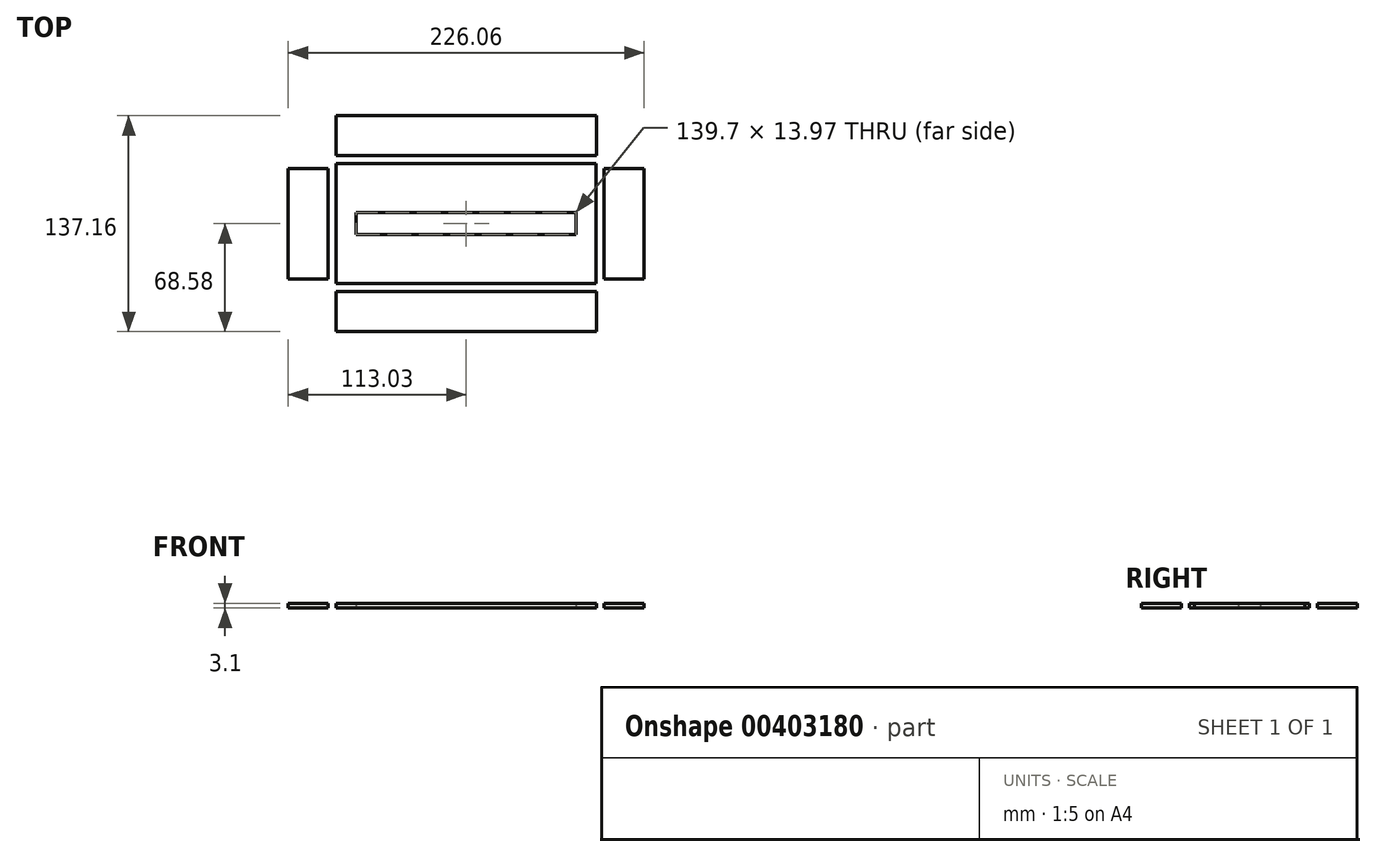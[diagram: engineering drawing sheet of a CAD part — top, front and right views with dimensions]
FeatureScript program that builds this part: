
annotation { "Feature Type Name" : "Feature", "Feature Type Description" : "" }
export const myFeature = defineFeature(function(context is Context, id is Id, definition is map)
    precondition{}
    {
        {
            var Q0;
            Q0=qCreatedBy(makeId("Top.planeOp"),FACE);
            var sketch = newSketch(context, id + "F0", { "sketchPlane" : qUnion([Q0])});
            skLineSegment(sketch, "E0.bottom", {"start": v(0, 0) * mm, "end": v(165.1, 0) * mm});
            skLineSegment(sketch, "E0.top", {"start": v(0, 76.2) * mm, "end": v(165.1, 76.2) * mm});
            skLineSegment(sketch, "E0.left", {"start": v(0, 0) * mm, "end": v(0, 76.2) * mm});
            skLineSegment(sketch, "E0.right", {"start": v(165.1, 0) * mm, "end": v(165.1, 76.2) * mm});
            skLineSegment(sketch, "E1.bottom", {"start": v(12.7, 45.09) * mm, "end": v(152.4, 45.09) * mm});
            skLineSegment(sketch, "E1.top", {"start": v(12.7, 31.12) * mm, "end": v(152.4, 31.12) * mm});
            skLineSegment(sketch, "E1.left", {"start": v(12.7, 45.09) * mm, "end": v(12.7, 31.12) * mm});
            skLineSegment(sketch, "E1.right", {"start": v(152.4, 45.09) * mm, "end": v(152.4, 31.12) * mm});
            skLineSegment(sketch, "E2", {"start": v(82.55, 45.09) * mm, "end": v(82.55, 31.12) * mm, "construction": true});
            skLineSegment(sketch, "E3", {"start": v(0, 38.1) * mm, "end": v(165.1, 38.1) * mm, "construction": true});
            skLineSegment(sketch, "E4", {"start": v(12.7, 38.1) * mm, "end": v(165.1, 38.1) * mm, "construction": true});
            skLineSegment(sketch, "E5", {"start": v(82.55, 0) * mm, "end": v(82.55, 76.2) * mm, "construction": true});
            skSolve(sketch);
        }
        {
            var Q0;
            Q0 = qSketchRegion(id + "F0", true);
            extrude(context, id + "F1", {"entities" : qUnion([Q0]), "depth" : 3.1 * mm});
        }
        {
            var Q0;
            Q0=makeQuery(id+"F1.opExtrude","CAP_FACE",FACE,{"disambiguationData":[OSD([sQuery(id+"F0.wireOp",EDGE,"E0.bottom"),sQuery(id+"F0.wireOp",EDGE,"E0.top"),sQuery(id+"F0.wireOp",EDGE,"E0.left"),sQuery(id+"F0.wireOp",EDGE,"E0.right"),sQuery(id+"F0.wireOp",EDGE,"E1.bottom"),sQuery(id+"F0.wireOp",EDGE,"E1.top"),sQuery(id+"F0.wireOp",EDGE,"E1.left"),sQuery(id+"F0.wireOp",EDGE,"E1.right")])],"isStart":false});
            var sketch = newSketch(context, id + "F2", { "sketchPlane" : qUnion([Q0])});
            skLineSegment(sketch, "E6.bottom", {"start": v(0, 76.2) * mm, "end": v(165.3, 76.2) * mm});
            skLineSegment(sketch, "E6.top", {"start": v(0, 106.68) * mm, "end": v(165.3, 106.68) * mm});
            skLineSegment(sketch, "E6.left", {"start": v(0, 81.28) * mm, "end": v(0, 106.68) * mm});
            skLineSegment(sketch, "E6.right", {"start": v(165.3, 81.28) * mm, "end": v(165.3, 106.68) * mm});
            skLineSegment(sketch, "E7.bottom", {"start": v(0, 0) * mm, "end": v(165.3, 0) * mm});
            skLineSegment(sketch, "E7.top", {"start": v(0, -30.48) * mm, "end": v(165.3, -30.48) * mm});
            skLineSegment(sketch, "E7.left", {"start": v(0, -5.08) * mm, "end": v(0, -30.48) * mm});
            skLineSegment(sketch, "E7.right", {"start": v(165.3, -5.08) * mm, "end": v(165.3, -30.48) * mm});
            skLineSegment(sketch, "E8.bottom", {"start": v(-5.08, 73.15) * mm, "end": v(-30.48, 73.15) * mm});
            skLineSegment(sketch, "E8.top", {"start": v(-5.08, 3.05) * mm, "end": v(-30.48, 3.05) * mm});
            skLineSegment(sketch, "E8.left", {"start": v(0, 73.15) * mm, "end": v(0, 3.05) * mm});
            skLineSegment(sketch, "E8.right", {"start": v(-30.48, 73.15) * mm, "end": v(-30.48, 3.05) * mm});
            skLineSegment(sketch, "E9.bottom", {"start": v(170.18, 3.05) * mm, "end": v(195.58, 3.05) * mm});
            skLineSegment(sketch, "E9.top", {"start": v(170.18, 73.15) * mm, "end": v(195.58, 73.15) * mm});
            skLineSegment(sketch, "E9.left", {"start": v(165.1, 3.05) * mm, "end": v(165.1, 73.15) * mm});
            skLineSegment(sketch, "E9.right", {"start": v(195.58, 3.05) * mm, "end": v(195.58, 73.15) * mm});
            skLineSegment(sketch, "E10", {"start": v(-5.08, 73.15) * mm, "end": v(-5.08, 3.05) * mm});
            skLineSegment(sketch, "E11", {"start": v(0, -5.08) * mm, "end": v(165.3, -5.08) * mm});
            skLineSegment(sketch, "E12", {"start": v(170.18, 3.05) * mm, "end": v(170.18, 73.15) * mm});
            skLineSegment(sketch, "E13", {"start": v(0, 81.28) * mm, "end": v(165.3, 81.28) * mm});
            skSolve(sketch);
        }
        {
            var Q0;
            Q0 = qSketchRegion(id + "F2", true);
            extrude(context, id + "F3", {"entities" : qUnion([Q0]), "oppositeDirection" : true, "depth" : 3.1 * mm});
        }
        {
            var Q0;
            Q0=makeQuery(id+"F3.opExtrude","SWEPT_BODY",BODY,{"disambiguationData":[OSD([sQuery(id+"F2.wireOp",EDGE,"E9.bottom"),sQuery(id+"F2.wireOp",EDGE,"E9.top"),sQuery(id+"F2.wireOp",EDGE,"E9.right"),sQuery(id+"F2.wireOp",EDGE,"E12")])]});
            var Q1;
            Q1=makeQuery(id+"F3.opExtrude","SWEPT_BODY",BODY,{"disambiguationData":[OSD([sQuery(id+"F2.wireOp",EDGE,"E8.bottom"),sQuery(id+"F2.wireOp",EDGE,"E8.top"),sQuery(id+"F2.wireOp",EDGE,"E8.right"),sQuery(id+"F2.wireOp",EDGE,"E10")])]});
            var Q2;
            Q2=makeQuery(id+"F3.opExtrude","SWEPT_BODY",BODY,{"disambiguationData":[OSD([sQuery(id+"F2.wireOp",EDGE,"E6.top"),sQuery(id+"F2.wireOp",EDGE,"E6.left"),sQuery(id+"F2.wireOp",EDGE,"E6.right"),sQuery(id+"F2.wireOp",EDGE,"E13")])]});
            var Q3;
            Q3=makeQuery(id+"F3.opExtrude","SWEPT_BODY",BODY,{"disambiguationData":[OSD([sQuery(id+"F2.wireOp",EDGE,"E7.top"),sQuery(id+"F2.wireOp",EDGE,"E7.left"),sQuery(id+"F2.wireOp",EDGE,"E7.right"),sQuery(id+"F2.wireOp",EDGE,"E11")])]});
            var Q4;
            Q4=makeQuery(id+"F1.opExtrude","SWEPT_BODY",BODY,{"disambiguationData":[OSD([sQuery(id+"F0.wireOp",EDGE,"E0.bottom"),sQuery(id+"F0.wireOp",EDGE,"E0.top"),sQuery(id+"F0.wireOp",EDGE,"E0.left"),sQuery(id+"F0.wireOp",EDGE,"E0.right"),sQuery(id+"F0.wireOp",EDGE,"E1.bottom"),sQuery(id+"F0.wireOp",EDGE,"E1.top"),sQuery(id+"F0.wireOp",EDGE,"E1.left"),sQuery(id+"F0.wireOp",EDGE,"E1.right")])]});
            transform(context, id + "F4", {"entities" : qUnion([Q0, Q1, Q2, Q3, Q4]), "transformType" : TransformType.TRANSLATION_3D, "dx" : 31.75 * mm, "dy" : 31.75 * mm, "dz" : 0 * mm, "makeCopy" : false});
        }
    });
